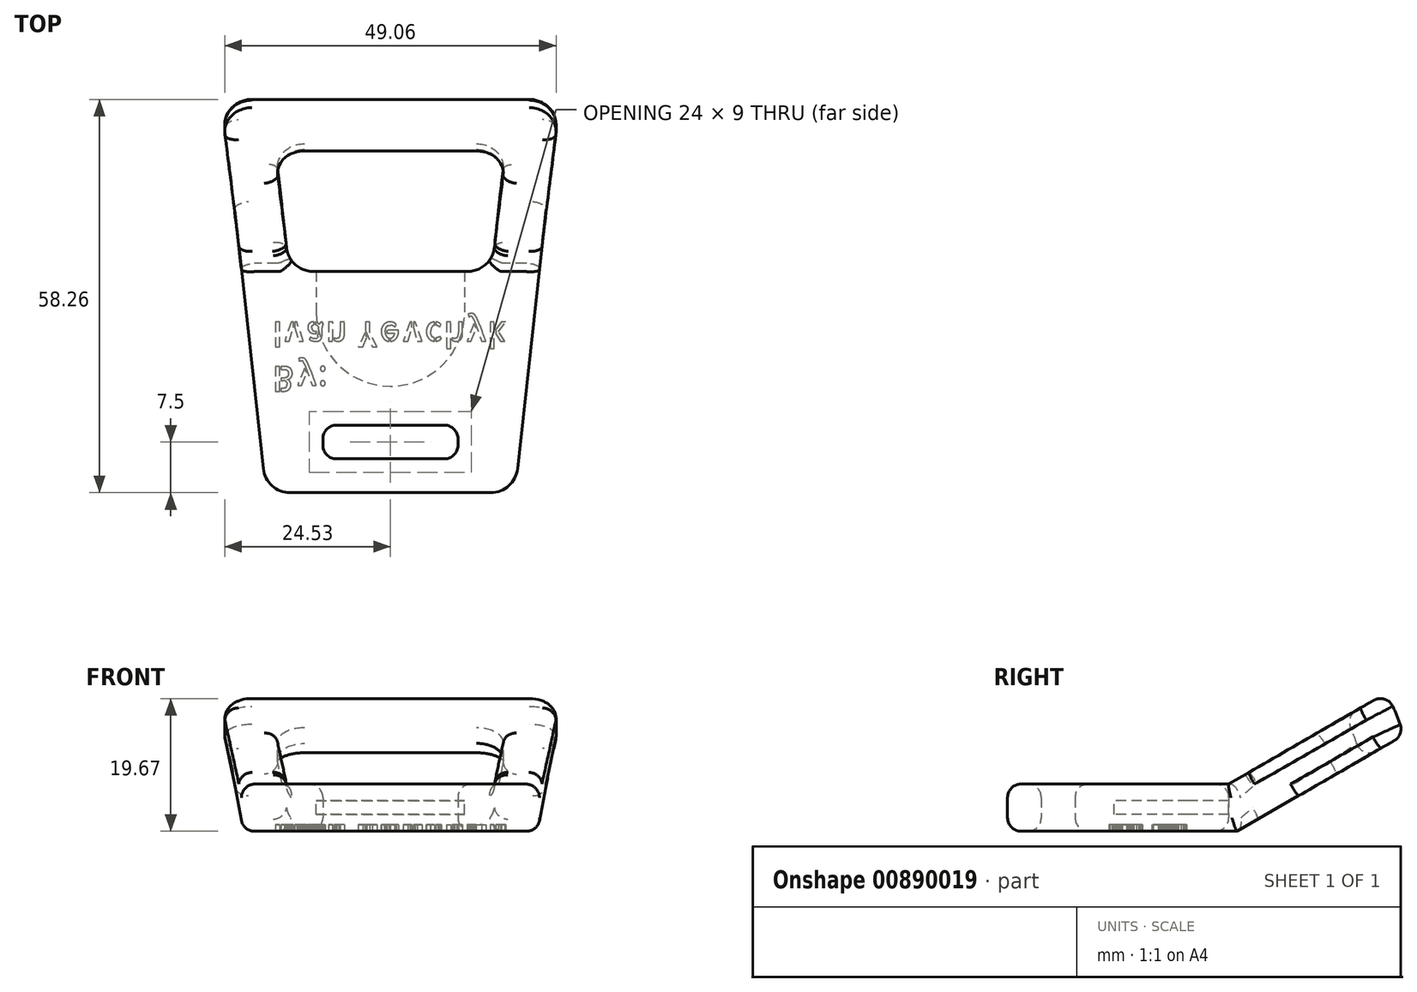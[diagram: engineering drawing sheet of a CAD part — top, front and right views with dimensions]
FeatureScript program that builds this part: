
annotation { "Feature Type Name" : "Feature", "Feature Type Description" : "" }
export const myFeature = defineFeature(function(context is Context, id is Id, definition is map)
    precondition{}
    {
        {
            var Q0;
            Q0=qCreatedBy(makeId("Top.planeOp"),FACE);
            var sketch = newSketch(context, id + "F0", { "sketchPlane" : qUnion([Q0])});
            skLineSegment(sketch, "E0", {"start": v(-20.54, 59.64) * mm, "end": v(20.54, 59.64) * mm});
            skLineSegment(sketch, "E1", {"start": v(24.51, 55.2) * mm, "end": v(18.83, 3.56) * mm});
            skLineSegment(sketch, "E2", {"start": v(14.85, 0) * mm, "end": v(-14.85, 0) * mm});
            skLineSegment(sketch, "E3", {"start": v(-18.83, 3.56) * mm, "end": v(-24.51, 55.2) * mm});
            skLineSegment(sketch, "E4", {"start": v(-12.72, 52.64) * mm, "end": v(12.72, 52.64) * mm});
            skLineSegment(sketch, "E5", {"start": v(16.7, 48.2) * mm, "end": v(15.4, 36.32) * mm});
            skLineSegment(sketch, "E6", {"start": v(11.42, 32.76) * mm, "end": v(-11.42, 32.76) * mm});
            skLineSegment(sketch, "E7", {"start": v(-15.4, 36.32) * mm, "end": v(-16.7, 48.2) * mm});
            skLineSegment(sketch, "E8.bottom", {"start": v(-8, 5) * mm, "end": v(8, 5) * mm});
            skLineSegment(sketch, "E8.top", {"start": v(-8, 10) * mm, "end": v(8, 10) * mm});
            skLineSegment(sketch, "E8.left", {"start": v(-10, 7) * mm, "end": v(-10, 8) * mm});
            skLineSegment(sketch, "E8.right", {"start": v(10, 7) * mm, "end": v(10, 8) * mm});
            skPoint(sketch, "E9.visualSharp", {"position": v(-25, 59.64) * mm});
            skArc(sketch, "E9.filletArc", {"start": v(-20.54, 59.64) * mm, "mid": v(-23.51, 58.3) * mm, "end": v(-24.51, 55.2) * mm});
            skPoint(sketch, "E10.visualSharp", {"position": v(25, 59.64) * mm});
            skArc(sketch, "E10.filletArc", {"start": v(24.51, 55.2) * mm, "mid": v(23.51, 58.3) * mm, "end": v(20.54, 59.64) * mm});
            skPoint(sketch, "E11.visualSharp", {"position": v(17.19, 52.64) * mm});
            skArc(sketch, "E11.filletArc", {"start": v(16.7, 48.2) * mm, "mid": v(15.7, 51.3) * mm, "end": v(12.72, 52.64) * mm});
            skPoint(sketch, "E12.visualSharp", {"position": v(-17.19, 52.64) * mm});
            skArc(sketch, "E12.filletArc", {"start": v(-12.72, 52.64) * mm, "mid": v(-15.7, 51.3) * mm, "end": v(-16.7, 48.2) * mm});
            skPoint(sketch, "E13.visualSharp", {"position": v(-15, 32.76) * mm});
            skArc(sketch, "E13.filletArc", {"start": v(-15.4, 36.32) * mm, "mid": v(-14.09, 33.78) * mm, "end": v(-11.42, 32.76) * mm});
            skPoint(sketch, "E14.visualSharp", {"position": v(15, 32.76) * mm});
            skArc(sketch, "E14.filletArc", {"start": v(11.42, 32.76) * mm, "mid": v(14.09, 33.78) * mm, "end": v(15.4, 36.32) * mm});
            skPoint(sketch, "E15.visualSharp", {"position": v(18.44, 0) * mm});
            skArc(sketch, "E15.filletArc", {"start": v(14.85, 0) * mm, "mid": v(17.52, 1.02) * mm, "end": v(18.83, 3.56) * mm});
            skPoint(sketch, "E16.visualSharp", {"position": v(-18.44, 0) * mm});
            skArc(sketch, "E16.filletArc", {"start": v(-18.83, 3.56) * mm, "mid": v(-17.52, 1.02) * mm, "end": v(-14.85, 0) * mm});
            skPoint(sketch, "E17.visualSharp", {"position": v(-10, 10) * mm});
            skArc(sketch, "E17.filletArc", {"start": v(-8, 10) * mm, "mid": v(-9.41, 9.41) * mm, "end": v(-10, 8) * mm});
            skPoint(sketch, "E18.visualSharp", {"position": v(-10, 5) * mm});
            skArc(sketch, "E18.filletArc", {"start": v(-10, 7) * mm, "mid": v(-9.41, 5.59) * mm, "end": v(-8, 5) * mm});
            skPoint(sketch, "E19.visualSharp", {"position": v(10, 10) * mm});
            skArc(sketch, "E19.filletArc", {"start": v(10, 8) * mm, "mid": v(9.41, 9.41) * mm, "end": v(8, 10) * mm});
            skPoint(sketch, "E20.visualSharp", {"position": v(10, 5) * mm});
            skArc(sketch, "E20.filletArc", {"start": v(8, 5) * mm, "mid": v(9.41, 5.59) * mm, "end": v(10, 7) * mm});
            skSolve(sketch);
        }
        {
            var Q0;
            Q0=makeQuery(id+"F0.imprint","IMPRINT",FACE,{"disambiguationData":[TD([[makeQuery(id+"F0.imprint","IMPRINT",EDGE,{"derivedFrom":sQuery(id+"F0.wireOp",EDGE,"E0")}),-1.0]])]});
            extrude(context, id + "F1", {"entities" : qUnion([Q0]), "depth" : 3.5 * mm, "offsetDistance" : 25 * mm});
        }
        {
            var Q0;
            Q0=makeQuery(id+"F1.opExtrude","CAP_FACE",FACE,{"disambiguationData":[OSD([sQuery(id+"F0.wireOp",EDGE,"E0"),sQuery(id+"F0.wireOp",EDGE,"E1"),sQuery(id+"F0.wireOp",EDGE,"E2"),sQuery(id+"F0.wireOp",EDGE,"E3"),sQuery(id+"F0.wireOp",EDGE,"E4"),sQuery(id+"F0.wireOp",EDGE,"E5"),sQuery(id+"F0.wireOp",EDGE,"E6"),sQuery(id+"F0.wireOp",EDGE,"E7"),sQuery(id+"F0.wireOp",EDGE,"E8.bottom"),sQuery(id+"F0.wireOp",EDGE,"E8.top"),sQuery(id+"F0.wireOp",EDGE,"E8.left"),sQuery(id+"F0.wireOp",EDGE,"E8.right"),sQuery(id+"F0.wireOp",EDGE,"E9.filletArc"),sQuery(id+"F0.wireOp",EDGE,"E10.filletArc"),sQuery(id+"F0.wireOp",EDGE,"E11.filletArc"),sQuery(id+"F0.wireOp",EDGE,"E12.filletArc"),sQuery(id+"F0.wireOp",EDGE,"E13.filletArc"),sQuery(id+"F0.wireOp",EDGE,"E14.filletArc"),sQuery(id+"F0.wireOp",EDGE,"E15.filletArc"),sQuery(id+"F0.wireOp",EDGE,"E16.filletArc"),sQuery(id+"F0.wireOp",EDGE,"E17.filletArc"),sQuery(id+"F0.wireOp",EDGE,"E18.filletArc"),sQuery(id+"F0.wireOp",EDGE,"E19.filletArc"),sQuery(id+"F0.wireOp",EDGE,"E20.filletArc")])],"isStart":false});
            var sketch = newSketch(context, id + "F2", { "sketchPlane" : qUnion([Q0])});
            skCircle(sketch, "E21", {"center": v(0, 26.76) * mm, "radius": 11 * mm});
            skPoint(sketch, "E21.centerSnap0", {"position": v(0, 32.76) * mm});
            skLineSegment(sketch, "E22", {"start": v(11, 32.76) * mm, "end": v(11, 26.76) * mm});
            skLineSegment(sketch, "E23", {"start": v(-11, 32.76) * mm, "end": v(-11, 26.76) * mm});
            skLineSegment(sketch, "E24", {"start": v(-11, 32.76) * mm, "end": v(11, 32.76) * mm});
            skSolve(sketch);
        }
        {
            var Q0;
            {var subQ3=sQuery(id+"F2.wireOp",EDGE,"E22");Q0=makeQuery(id+"F2.imprint","IMPRINT",FACE,{"disambiguationData":[TD([[makeQuery(id+"F2.imprint","IMPRINT",EDGE,{"derivedFrom":subQ3}),1.0]])]});}
            var Q1;
            {var subQ0=sQuery(id+"F2.wireOp",EDGE,"E21");var subQ1=makeQuery(id+"F2.imprint","INTERSECT",VERTEX,{"derivedFrom":[subQ0,sQuery(id+"F2.wireOp",EDGE,"E22")]});Q1=makeQuery(id+"F2.imprint","IMPRINT",FACE,{"disambiguationData":[TD([[makeQuery(id+"F2.imprint","IMPRINT",EDGE,{"disambiguationData":[TD([[subQ1,-1.0]])],"derivedFrom":subQ0}),1.0]])]});}
            var Q2;
            {var subQ0=sQuery(id+"F2.wireOp",EDGE,"E23");Q2=makeQuery(id+"F2.imprint","IMPRINT",FACE,{"disambiguationData":[TD([[makeQuery(id+"F2.imprint","IMPRINT",EDGE,{"derivedFrom":subQ0}),1.0]])]});}
            var Q3;
            {var subQ0=sQuery(id+"F2.wireOp",EDGE,"E22");Q3=makeQuery(id+"F2.imprint","IMPRINT",FACE,{"disambiguationData":[TD([[makeQuery(id+"F2.imprint","IMPRINT",EDGE,{"derivedFrom":subQ0}),-1.0]])]});}
            extrude(context, id + "F3", {"entities" : qUnion([Q0, Q1, Q2, Q3]), "operationType" : NewBodyOperationType.ADD, "depth" : 3.5 * mm, "offsetDistance" : 25 * mm});
        }
        {
            var Q0;
            Q0 = qSketchRegion(id + "F2", true);
            extrude(context, id + "F4", {"entities" : qUnion([Q0]), "operationType" : NewBodyOperationType.REMOVE, "oppositeDirection" : true, "depth" : 2 * mm, "offsetDistance" : 25 * mm, "symmetric" : true});
        }
        {
            var Q0;
            Q0=makeQuery(id+"F3.opExtrude","CAP_FACE",FACE,{"disambiguationData":[OSD([sQuery(id+"F0.wireOp",EDGE,"E0"),sQuery(id+"F0.wireOp",EDGE,"E1"),sQuery(id+"F0.wireOp",EDGE,"E2"),sQuery(id+"F0.wireOp",EDGE,"E3"),sQuery(id+"F0.wireOp",EDGE,"E4"),sQuery(id+"F0.wireOp",EDGE,"E5"),sQuery(id+"F0.wireOp",EDGE,"E6"),sQuery(id+"F0.wireOp",EDGE,"E7"),sQuery(id+"F0.wireOp",EDGE,"E8.bottom"),sQuery(id+"F0.wireOp",EDGE,"E8.top"),sQuery(id+"F0.wireOp",EDGE,"E8.left"),sQuery(id+"F0.wireOp",EDGE,"E8.right"),sQuery(id+"F0.wireOp",EDGE,"E9.filletArc"),sQuery(id+"F0.wireOp",EDGE,"E10.filletArc"),sQuery(id+"F0.wireOp",EDGE,"E11.filletArc"),sQuery(id+"F0.wireOp",EDGE,"E12.filletArc"),sQuery(id+"F0.wireOp",EDGE,"E13.filletArc"),sQuery(id+"F0.wireOp",EDGE,"E14.filletArc"),sQuery(id+"F0.wireOp",EDGE,"E15.filletArc"),sQuery(id+"F0.wireOp",EDGE,"E16.filletArc"),sQuery(id+"F0.wireOp",EDGE,"E17.filletArc"),sQuery(id+"F0.wireOp",EDGE,"E18.filletArc"),sQuery(id+"F0.wireOp",EDGE,"E19.filletArc"),sQuery(id+"F0.wireOp",EDGE,"E20.filletArc"),sQuery(id+"F2.wireOp",EDGE,"E24")])],"isStart":false});
            var sketch = newSketch(context, id + "F5", { "sketchPlane" : qUnion([Q0])});
            skLineSegment(sketch, "E25", {"start": v(22.04, 32.76) * mm, "end": v(-22.04, 32.76) * mm});
            skSolve(sketch);
        }
        {
            var Q0;
            Q0=makeQuery(id+"F5.imprint","IMPRINT",FACE,{"disambiguationData":[TD([[makeQuery(id+"F5.imprint","IMPRINT",EDGE,{"derivedFrom":makeQuery(id+"F3.opExtrude","CAP_EDGE",EDGE,{"disambiguationData":[OSD([sQuery(id+"F0.wireOp",EDGE,"E0")])],"isStart":false})}),-1.0]])]});
            var Q1;
            Q1=sQuery(id+"F5.wireOp",EDGE,"E25");
            revolve(context, id + "F6", {"operationType" : NewBodyOperationType.ADD, "surfaceOperationType" : NewSurfaceOperationType.NEW, "entities" : qUnion([Q0]), "axis" : qUnion([Q1]), "revolveType" : RevolveType.ONE_DIRECTION, "oppositeDirection" : true, "angle" : 30 * degree});
        }
        {
            var Q0;
            Q0=makeQuery(id+"F1.opExtrude","CAP_FACE",FACE,{"disambiguationData":[OSD([sQuery(id+"F0.wireOp",EDGE,"E0"),sQuery(id+"F0.wireOp",EDGE,"E1"),sQuery(id+"F0.wireOp",EDGE,"E2"),sQuery(id+"F0.wireOp",EDGE,"E3"),sQuery(id+"F0.wireOp",EDGE,"E4"),sQuery(id+"F0.wireOp",EDGE,"E5"),sQuery(id+"F0.wireOp",EDGE,"E6"),sQuery(id+"F0.wireOp",EDGE,"E7"),sQuery(id+"F0.wireOp",EDGE,"E8.bottom"),sQuery(id+"F0.wireOp",EDGE,"E8.top"),sQuery(id+"F0.wireOp",EDGE,"E8.left"),sQuery(id+"F0.wireOp",EDGE,"E8.right"),sQuery(id+"F0.wireOp",EDGE,"E9.filletArc"),sQuery(id+"F0.wireOp",EDGE,"E10.filletArc"),sQuery(id+"F0.wireOp",EDGE,"E11.filletArc"),sQuery(id+"F0.wireOp",EDGE,"E12.filletArc"),sQuery(id+"F0.wireOp",EDGE,"E13.filletArc"),sQuery(id+"F0.wireOp",EDGE,"E14.filletArc"),sQuery(id+"F0.wireOp",EDGE,"E15.filletArc"),sQuery(id+"F0.wireOp",EDGE,"E16.filletArc"),sQuery(id+"F0.wireOp",EDGE,"E17.filletArc"),sQuery(id+"F0.wireOp",EDGE,"E18.filletArc"),sQuery(id+"F0.wireOp",EDGE,"E19.filletArc"),sQuery(id+"F0.wireOp",EDGE,"E20.filletArc")])],"isStart":true});
            var sketch = newSketch(context, id + "F7", { "sketchPlane" : qUnion([Q0])});
            skLineSegment(sketch, "E26.bottom", {"start": v(31.73, -34) * mm, "end": v(-29.98, -34) * mm});
            skLineSegment(sketch, "E26.top", {"start": v(31.73, -66.97) * mm, "end": v(-29.98, -66.97) * mm});
            skLineSegment(sketch, "E26.left", {"start": v(31.73, -34) * mm, "end": v(31.73, -66.97) * mm});
            skLineSegment(sketch, "E26.right", {"start": v(-29.98, -34) * mm, "end": v(-29.98, -66.97) * mm});
            skSolve(sketch);
        }
        {
            var Q0;
            Q0 = qSketchRegion(id + "F7", true);
            var Q1;
            Q1=sQuery(id+"F7.wireOp",EDGE,"E26.bottom");
            revolve(context, id + "F8", {"operationType" : NewBodyOperationType.REMOVE, "surfaceOperationType" : NewSurfaceOperationType.NEW, "entities" : qUnion([Q0]), "axis" : qUnion([Q1]), "revolveType" : RevolveType.ONE_DIRECTION, "oppositeDirection" : true, "angle" : 30 * degree});
        }
        {
            var Q0;
            Q0=makeQuery(id+"F8.boolean.opBoolean","INTERSECT",EDGE,{"derivedFrom":[makeQuery(id+"F6.opRevolve","SWEPT_FACE",FACE,{"disambiguationData":[OSD([sQuery(id+"F0.wireOp",EDGE,"E3")])]}),makeQuery(id+"F8.opRevolve","CAP_FACE",FACE,{"disambiguationData":[OSD([sQuery(id+"F7.wireOp",EDGE,"E26.bottom"),sQuery(id+"F7.wireOp",EDGE,"E26.top"),sQuery(id+"F7.wireOp",EDGE,"E26.left"),sQuery(id+"F7.wireOp",EDGE,"E26.right")])],"isStart":false})]});
            var Q1;
            Q1=makeQuery(id+"F1.opExtrude","CAP_EDGE",EDGE,{"disambiguationData":[OSD([sQuery(id+"F0.wireOp",EDGE,"E6")])],"isStart":true});
            var Q2;
            {var subQ0=sQuery(id+"F0.wireOp",EDGE,"E7");Q2=makeQuery(id+"F8.boolean.opBoolean","INTERSECT",EDGE,{"derivedFrom":[makeQuery(id+"F3.boolean.opBoolean","MERGE",FACE,{"derivedFrom":[makeQuery(id+"F1.opExtrude","SWEPT_FACE",FACE,{"disambiguationData":[OSD([subQ0])]}),makeQuery(id+"F3.opExtrude","SWEPT_FACE",FACE,{"disambiguationData":[OSD([subQ0])]})]}),makeQuery(id+"F8.opRevolve","CAP_FACE",FACE,{"disambiguationData":[OSD([sQuery(id+"F7.wireOp",EDGE,"E26.bottom"),sQuery(id+"F7.wireOp",EDGE,"E26.top"),sQuery(id+"F7.wireOp",EDGE,"E26.left"),sQuery(id+"F7.wireOp",EDGE,"E26.right")])],"isStart":false})]});}
            var Q3;
            Q3=makeQuery(id+"F1.opExtrude","CAP_EDGE",EDGE,{"disambiguationData":[OSD([sQuery(id+"F0.wireOp",EDGE,"E1")])],"isStart":true});
            var Q4;
            Q4=makeQuery(id+"F1.opExtrude","CAP_EDGE",EDGE,{"disambiguationData":[OSD([sQuery(id+"F0.wireOp",EDGE,"E8.top")])],"isStart":true});
            var Q5;
            Q5=makeQuery(id+"F6.opRevolve","CAP_EDGE",EDGE,{"disambiguationData":[OSD([sQuery(id+"F0.wireOp",EDGE,"E5")])],"isStart":false});
            var Q6;
            Q6=makeQuery(id+"F3.opExtrude","CAP_EDGE",EDGE,{"disambiguationData":[OSD([sQuery(id+"F0.wireOp",EDGE,"E6"),sQuery(id+"F2.wireOp",EDGE,"E24")])],"isStart":false});
            var Q7;
            Q7=makeQuery(id+"F6.opRevolve","CAP_EDGE",EDGE,{"disambiguationData":[OSD([sQuery(id+"F0.wireOp",EDGE,"E1")])],"isStart":false});
            var Q8;
            Q8=makeQuery(id+"F6.boolean.opBoolean","SPLIT",EDGE,{"derivedFrom":makeQuery(id+"F3.opExtrude","CAP_EDGE",EDGE,{"disambiguationData":[OSD([sQuery(id+"F0.wireOp",EDGE,"E1")])],"isStart":false})});
            var Q9;
            Q9=makeQuery(id+"F3.opExtrude","CAP_EDGE",EDGE,{"disambiguationData":[OSD([sQuery(id+"F0.wireOp",EDGE,"E8.bottom")])],"isStart":false});
            fillet(context, id + "F9", {"entities" : qUnion([Q0, Q1, Q2, Q3, Q4, Q5, Q6, Q7, Q8, Q9]), "radius" : 2 * mm, "tangentPropagation" : true, "allowEdgeOverflow" : false});
        }
        {
            var Q0;
            Q0=makeQuery(id+"F1.opExtrude","CAP_FACE",FACE,{"disambiguationData":[OSD([sQuery(id+"F0.wireOp",EDGE,"E0"),sQuery(id+"F0.wireOp",EDGE,"E1"),sQuery(id+"F0.wireOp",EDGE,"E2"),sQuery(id+"F0.wireOp",EDGE,"E3"),sQuery(id+"F0.wireOp",EDGE,"E4"),sQuery(id+"F0.wireOp",EDGE,"E5"),sQuery(id+"F0.wireOp",EDGE,"E6"),sQuery(id+"F0.wireOp",EDGE,"E7"),sQuery(id+"F0.wireOp",EDGE,"E8.bottom"),sQuery(id+"F0.wireOp",EDGE,"E8.top"),sQuery(id+"F0.wireOp",EDGE,"E8.left"),sQuery(id+"F0.wireOp",EDGE,"E8.right"),sQuery(id+"F0.wireOp",EDGE,"E9.filletArc"),sQuery(id+"F0.wireOp",EDGE,"E10.filletArc"),sQuery(id+"F0.wireOp",EDGE,"E11.filletArc"),sQuery(id+"F0.wireOp",EDGE,"E12.filletArc"),sQuery(id+"F0.wireOp",EDGE,"E13.filletArc"),sQuery(id+"F0.wireOp",EDGE,"E14.filletArc"),sQuery(id+"F0.wireOp",EDGE,"E15.filletArc"),sQuery(id+"F0.wireOp",EDGE,"E16.filletArc"),sQuery(id+"F0.wireOp",EDGE,"E17.filletArc"),sQuery(id+"F0.wireOp",EDGE,"E18.filletArc"),sQuery(id+"F0.wireOp",EDGE,"E19.filletArc"),sQuery(id+"F0.wireOp",EDGE,"E20.filletArc")])],"isStart":true});
            var sketch = newSketch(context, id + "F10", { "sketchPlane" : qUnion([Q0])});
            skText(sketch, "E27", { "text": "By:\nIvan Yevchyk", "fontName": "AllertaStencil-Regular.ttf"});
            const initialGuessF10  = {"E27": [-0.0175, -0.0187, 1, 0, 0.0037]};
            skSetInitialGuess(sketch, initialGuessF10);
            skSolve(sketch);
        }
        {
            var Q0;
            Q0 = qSketchRegion(id + "F10", true);
            extrude(context, id + "F11", {"entities" : qUnion([Q0]), "operationType" : NewBodyOperationType.REMOVE, "oppositeDirection" : true, "depth" : 1 * mm, "offsetDistance" : 25 * mm});
        }
    });
